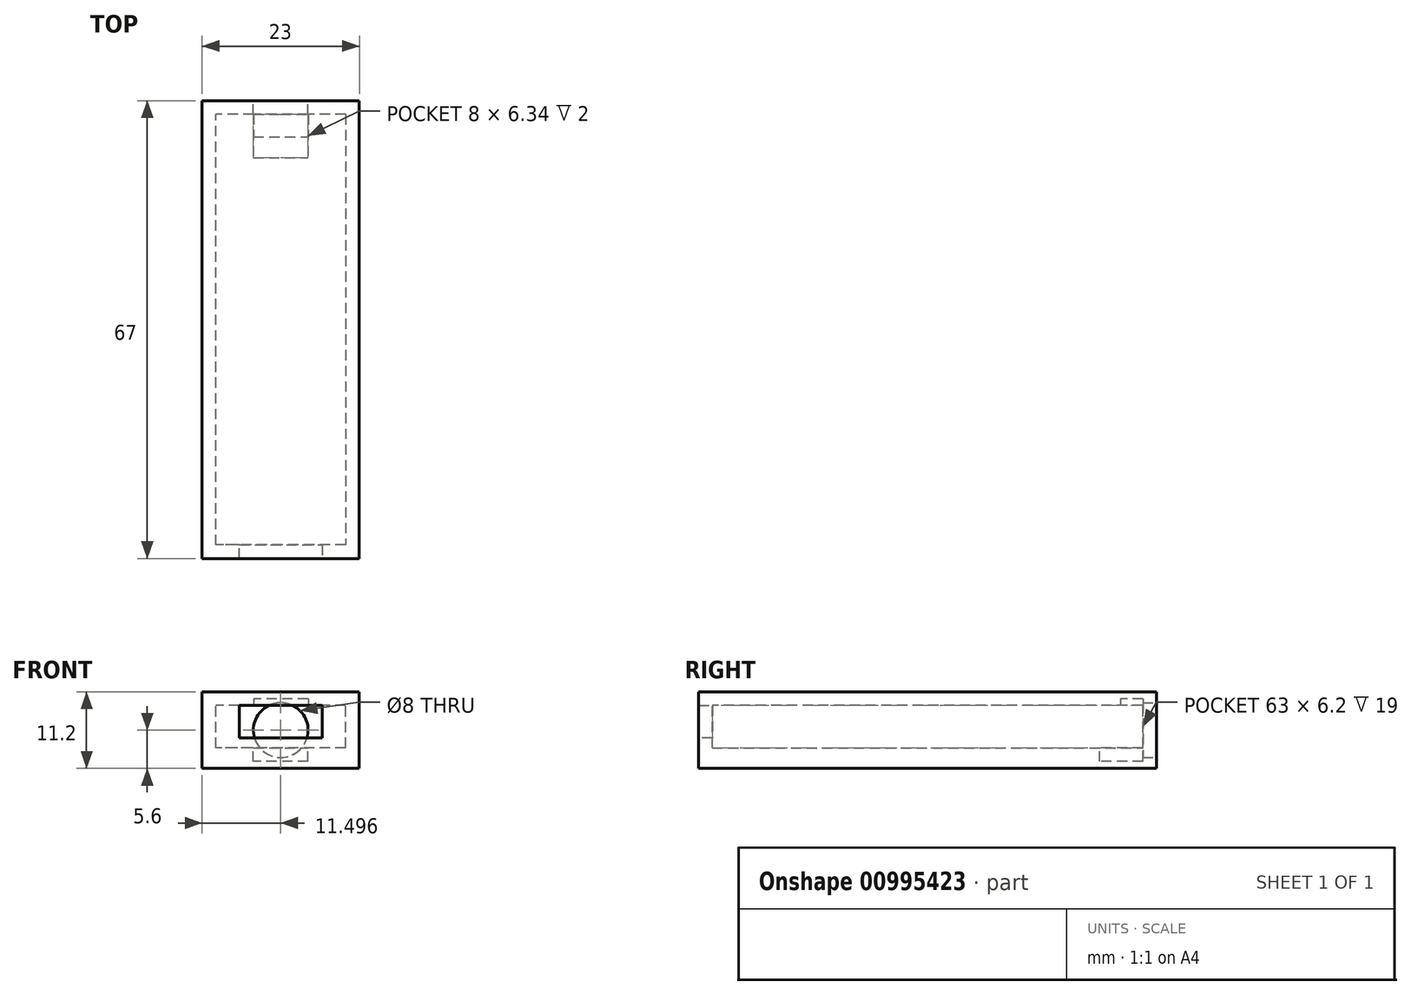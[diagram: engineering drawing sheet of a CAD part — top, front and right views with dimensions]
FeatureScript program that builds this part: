
annotation { "Feature Type Name" : "Feature", "Feature Type Description" : "" }
export const myFeature = defineFeature(function(context is Context, id is Id, definition is map)
    precondition{}
    {
        {
            var Q0;
            Q0=qCreatedBy(makeId("Top.planeOp"),FACE);
            var sketch = newSketch(context, id + "F0", { "sketchPlane" : qUnion([Q0])});
            skLineSegment(sketch, "E0.bottom", {"start": v(17.43, -33.5) * mm, "end": v(-5.57, -33.5) * mm});
            skLineSegment(sketch, "E0.top", {"start": v(17.43, 33.5) * mm, "end": v(-5.57, 33.5) * mm});
            skLineSegment(sketch, "E0.left", {"start": v(17.43, -33.5) * mm, "end": v(17.43, 33.5) * mm});
            skLineSegment(sketch, "E0.right", {"start": v(-5.57, -33.5) * mm, "end": v(-5.57, 33.5) * mm});
            skPoint(sketch, "E0.middle", {"position": v(5.93, 0) * mm});
            skSolve(sketch);
        }
        {
            var Q0;
            Q0 = qSketchRegion(id + "F0", true);
            extrude(context, id + "F1", {"entities" : qUnion([Q0]), "depth" : 11.2 * mm, "offsetDistance" : 25 * mm});
        }
        {
            var Q0;
            Q0=makeQuery(id+"F1.opExtrude","CAP_FACE",FACE,{"disambiguationData":[OSD([sQuery(id+"F0.wireOp",EDGE,"E0.bottom"),sQuery(id+"F0.wireOp",EDGE,"E0.top"),sQuery(id+"F0.wireOp",EDGE,"E0.left"),sQuery(id+"F0.wireOp",EDGE,"E0.right")])],"isStart":false});
            var sketch = newSketch(context, id + "F2", { "sketchPlane" : qUnion([Q0])});
            skLineSegment(sketch, "E1.0", {"start": v(-3.57, -31.5) * mm, "end": v(-3.57, 31.5) * mm});
            skLineSegment(sketch, "E1.1", {"start": v(15.43, -31.5) * mm, "end": v(-3.57, -31.5) * mm});
            skLineSegment(sketch, "E1.2", {"start": v(15.43, -31.5) * mm, "end": v(15.43, 31.5) * mm});
            skLineSegment(sketch, "E1.3", {"start": v(15.43, 31.5) * mm, "end": v(-3.57, 31.5) * mm});
            skSolve(sketch);
        }
        {
            var Q0;
            Q0=makeQuery(id+"F2.imprint","IMPRINT",FACE,{"disambiguationData":[TD([[makeQuery(id+"F2.imprint","IMPRINT",EDGE,{"derivedFrom":sQuery(id+"F2.wireOp",EDGE,"E1.0")}),-1.0]])]});
            extrude(context, id + "F3", {"entities" : qUnion([Q0]), "operationType" : NewBodyOperationType.REMOVE, "oppositeDirection" : true, "depth" : 9.2 * mm, "offsetDistance" : 25 * mm});
        }
        {
            var Q0;
            Q0=makeQuery(id+"F1.opExtrude","SWEPT_FACE",FACE,{"disambiguationData":[OSD([sQuery(id+"F0.wireOp",EDGE,"E0.bottom")])]});
            var sketch = newSketch(context, id + "F4", { "sketchPlane" : qUnion([Q0])});
            skLineSegment(sketch, "E2.bottom", {"start": v(11.98, 4.45) * mm, "end": v(-0.12, 4.45) * mm});
            skLineSegment(sketch, "E2.top", {"start": v(11.98, 17.95) * mm, "end": v(-0.12, 17.95) * mm});
            skLineSegment(sketch, "E2.left", {"start": v(11.98, 4.45) * mm, "end": v(11.98, 17.95) * mm});
            skLineSegment(sketch, "E2.right", {"start": v(-0.12, 4.45) * mm, "end": v(-0.12, 17.95) * mm});
            skPoint(sketch, "E2.middle", {"position": v(5.93, 11.2) * mm});
            skSolve(sketch);
        }
        {
            var Q0;
            Q0 = qSketchRegion(id + "F4", true);
            extrude(context, id + "F5", {"entities" : qUnion([Q0]), "operationType" : NewBodyOperationType.REMOVE, "oppositeDirection" : true, "depth" : 12 * mm, "offsetDistance" : 25 * mm});
        }
        {
            var Q0;
            Q0=makeQuery(id+"F1.opExtrude","SWEPT_FACE",FACE,{"disambiguationData":[OSD([sQuery(id+"F0.wireOp",EDGE,"E0.top")])]});
            var sketch = newSketch(context, id + "F6", { "sketchPlane" : qUnion([Q0])});
            skLineSegment(sketch, "E3", {"start": v(-17.43, 5.6) * mm, "end": v(5.57, 5.6) * mm});
            skPoint(sketch, "E4", {"position": v(-5.93, 5.6) * mm});
            skLineSegment(sketch, "E5", {"start": v(-5.93, 11.2) * mm, "end": v(-5.93, 0) * mm});
            skCircle(sketch, "E6", {"center": v(-5.93, 5.6) * mm, "radius": 4 * mm});
            skSolve(sketch);
        }
        {
            var Q0;
            Q0 = qSketchRegion(id + "F6", true);
            extrude(context, id + "F7", {"entities" : qUnion([Q0]), "operationType" : NewBodyOperationType.REMOVE, "oppositeDirection" : true, "depth" : 2 * mm, "offsetDistance" : 25 * mm});
        }
        {
            var Q0;
            Q0=makeQuery(id+"F3.boolean.opBoolean","COPY",FACE,{"derivedFrom":makeQuery(id+"F3.opExtrude","CAP_FACE",FACE,{"disambiguationData":[OSD([sQuery(id+"F2.wireOp",EDGE,"E1.0"),sQuery(id+"F2.wireOp",EDGE,"E1.1"),sQuery(id+"F2.wireOp",EDGE,"E1.2"),sQuery(id+"F2.wireOp",EDGE,"E1.3")])],"isStart":false})});
            var sketch = newSketch(context, id + "F8", { "sketchPlane" : qUnion([Q0])});
            skLineSegment(sketch, "E7.bottom", {"start": v(1.93, 31.5) * mm, "end": v(9.93, 31.5) * mm});
            skLineSegment(sketch, "E7.top", {"start": v(1.93, 25.16) * mm, "end": v(9.93, 25.16) * mm});
            skLineSegment(sketch, "E7.left", {"start": v(1.93, 31.5) * mm, "end": v(1.93, 25.16) * mm});
            skLineSegment(sketch, "E7.right", {"start": v(9.93, 31.5) * mm, "end": v(9.93, 25.16) * mm});
            skSolve(sketch);
        }
        {
            var Q0;
            Q0=makeQuery(id+"F8.imprint","IMPRINT",FACE,{"disambiguationData":[TD([[makeQuery(id+"F8.imprint","IMPRINT",EDGE,{"derivedFrom":sQuery(id+"F8.wireOp",EDGE,"E7.top")}),1.0]])]});
            extrude(context, id + "F9", {"entities" : qUnion([Q0]), "operationType" : NewBodyOperationType.REMOVE, "oppositeDirection" : true, "depth" : 1 * mm, "offsetDistance" : 25 * mm});
        }
        {
            var Q0;
            Q0=makeQuery(id+"F3.boolean.opBoolean","COPY",FACE,{"derivedFrom":makeQuery(id+"F3.opExtrude","CAP_FACE",FACE,{"disambiguationData":[OSD([sQuery(id+"F2.wireOp",EDGE,"E1.0"),sQuery(id+"F2.wireOp",EDGE,"E1.1"),sQuery(id+"F2.wireOp",EDGE,"E1.2"),sQuery(id+"F2.wireOp",EDGE,"E1.3")])],"isStart":false})});
            var sketch = newSketch(context, id + "F10", { "sketchPlane" : qUnion([Q0])});
            skSolve(sketch);
        }
        {
            var Q0;
            {var subQ2=sQuery(id+"F2.wireOp",EDGE,"E1.0");Q0=makeQuery(id+"F10.imprint","IMPRINT",FACE,{"disambiguationData":[TD([[makeQuery(id+"F10.imprint","IMPRINT",EDGE,{"derivedFrom":makeQuery(id+"F3.boolean.opBoolean","COPY",EDGE,{"derivedFrom":makeQuery(id+"F3.opExtrude","CAP_EDGE",EDGE,{"disambiguationData":[OSD([subQ2])],"isStart":false})})}),-1.0]])]});}
            extrude(context, id + "F11", {"entities" : qUnion([Q0]), "operationType" : NewBodyOperationType.ADD, "depth" : 1 * mm, "offsetDistance" : 25 * mm});
        }
        {
            var Q0;
            Q0=makeQuery(id+"F3.boolean.opBoolean","COPY",FACE,{"derivedFrom":makeQuery(id+"F3.opExtrude","SWEPT_FACE",FACE,{"disambiguationData":[OSD([sQuery(id+"F2.wireOp",EDGE,"E1.0")])]})});
            var sketch = newSketch(context, id + "F12", { "sketchPlane" : qUnion([Q0])});
            skLineSegment(sketch, "E8.0", {"start": v(-31.5, 9.2) * mm, "end": v(31.5, 9.2) * mm});
            skSolve(sketch);
        }
        {
            var Q0;
            {var subQ0=sQuery(id+"F12.wireOp",EDGE,"E8.0");Q0=makeQuery(id+"F12.imprint","IMPRINT",FACE,{"disambiguationData":[TD([[makeQuery(id+"F12.imprint","IMPRINT",EDGE,{"derivedFrom":subQ0}),1.0]])]});}
            extrude(context, id + "F13", {"entities" : qUnion([Q0]), "operationType" : NewBodyOperationType.ADD, "depth" : 21 * mm, "offsetDistance" : 25 * mm});
        }
        {
            var Q0;
            Q0=makeQuery(id+"F13.opExtrude","SWEPT_FACE",FACE,{"disambiguationData":[OSD([sQuery(id+"F2.wireOp",EDGE,"E1.0"),sQuery(id+"F2.wireOp",EDGE,"E1.1")])]});
            extrude(context, id + "F14", {"entities" : qUnion([Q0]), "operationType" : NewBodyOperationType.ADD, "depth" : 2 * mm, "offsetDistance" : 25 * mm});
        }
        {
            var Q0;
            {var subQ0=sQuery(id+"F12.wireOp",EDGE,"E8.0");Q0=makeQuery(id+"F14.boolean.opBoolean","MERGE",FACE,{"derivedFrom":[makeQuery(id+"F13.opExtrude","SWEPT_FACE",FACE,{"disambiguationData":[OSD([subQ0])]}),makeQuery(id+"F14.opExtrude","SWEPT_FACE",FACE,{"disambiguationData":[OSD([sQuery(id+"F2.wireOp",EDGE,"E1.0"),sQuery(id+"F2.wireOp",EDGE,"E1.1"),subQ0])]})]});}
            var sketch = newSketch(context, id + "F15", { "sketchPlane" : qUnion([Q0])});
            skLineSegment(sketch, "E9.bottom", {"start": v(1.96, -31.5) * mm, "end": v(9.95, -31.5) * mm});
            skLineSegment(sketch, "E9.top", {"start": v(1.96, -28.2) * mm, "end": v(9.95, -28.2) * mm});
            skLineSegment(sketch, "E9.left", {"start": v(1.96, -31.5) * mm, "end": v(1.96, -28.2) * mm});
            skLineSegment(sketch, "E9.right", {"start": v(9.95, -31.5) * mm, "end": v(9.95, -28.2) * mm});
            skSolve(sketch);
        }
        {
            var Q0;
            Q0 = qSketchRegion(id + "F15", true);
            extrude(context, id + "F16", {"entities" : qUnion([Q0]), "operationType" : NewBodyOperationType.REMOVE, "oppositeDirection" : true, "depth" : 1 * mm, "offsetDistance" : 25 * mm});
        }
    });
